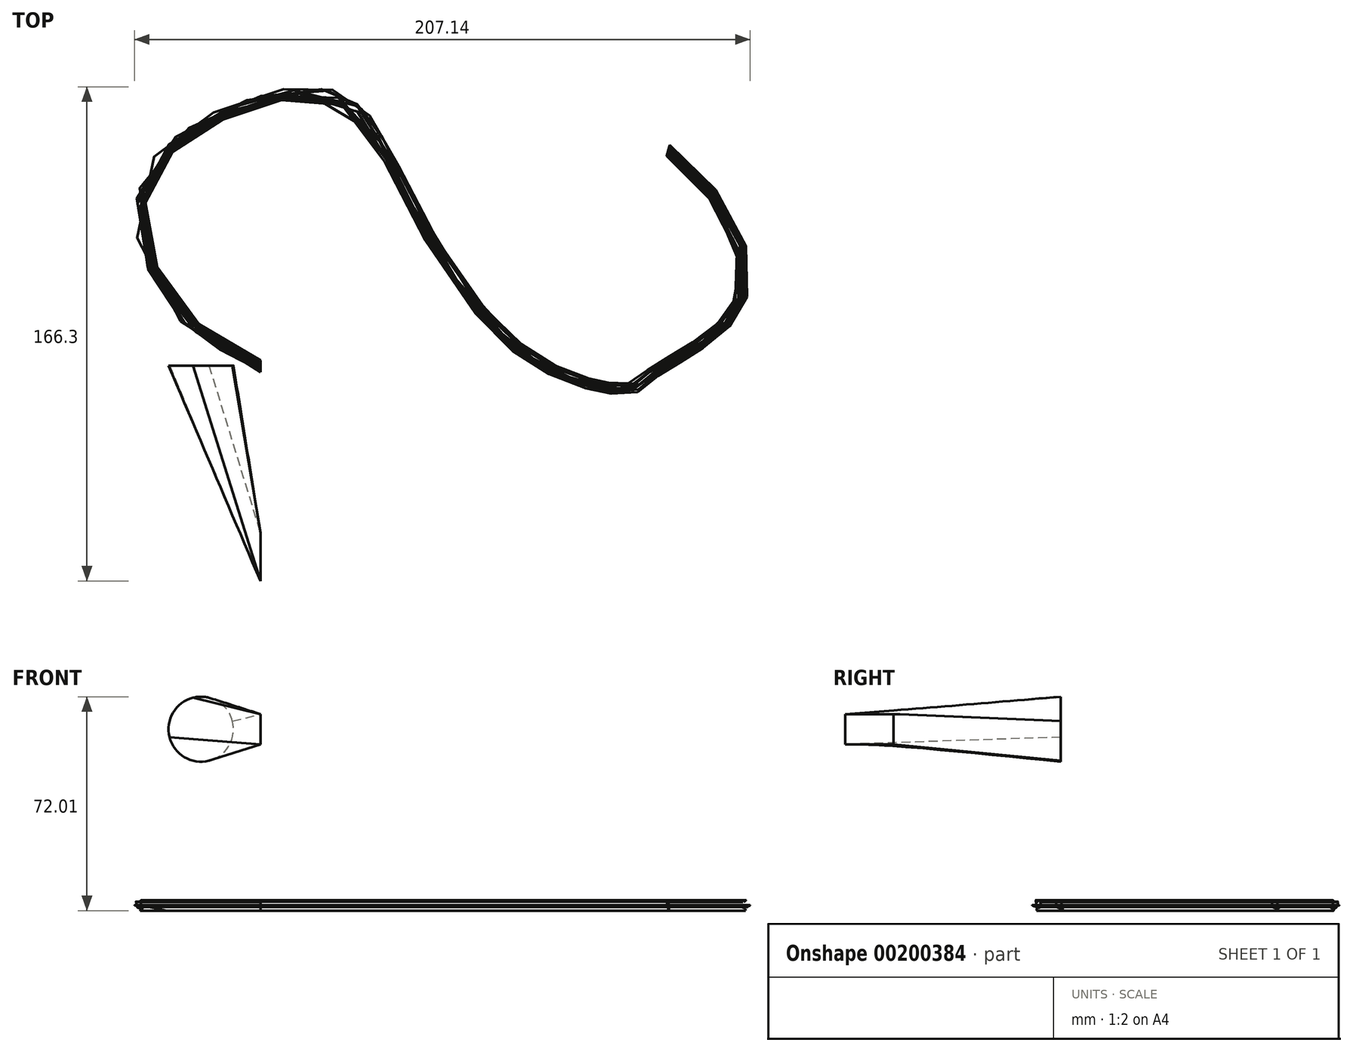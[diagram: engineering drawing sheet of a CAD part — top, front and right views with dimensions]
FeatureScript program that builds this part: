
annotation { "Feature Type Name" : "Feature", "Feature Type Description" : "" }
export const myFeature = defineFeature(function(context is Context, id is Id, definition is map)
    precondition{}
    {
        {
            var Q0;
            Q0=qCreatedBy(makeId("Front.planeOp"),FACE);
            var sketch = newSketch(context, id + "F0", { "sketchPlane" : qUnion([Q0])});
            skCircle(sketch, "E0", {"center": v(-20, 59.3) * mm, "radius": 10.93 * mm});
            skSolve(sketch);
        }
        {
            var Q0;
            Q0=qCreatedBy(makeId("Right.planeOp"),FACE);
            var sketch = newSketch(context, id + "F1", { "sketchPlane" : qUnion([Q0])});
            skLineSegment(sketch, "E1.bottom", {"start": v(-56.3, 64.38) * mm, "end": v(-72.5, 64.38) * mm});
            skLineSegment(sketch, "E1.top", {"start": v(-56.3, 54.2) * mm, "end": v(-72.5, 54.2) * mm});
            skLineSegment(sketch, "E1.left", {"start": v(-56.3, 64.38) * mm, "end": v(-56.3, 54.2) * mm});
            skLineSegment(sketch, "E1.right", {"start": v(-72.5, 64.38) * mm, "end": v(-72.5, 54.2) * mm});
            skSolve(sketch);
        }
        {
            var Q0;
            Q0=makeQuery(id+"F0.imprint","IMPRINT",FACE,{"disambiguationData":[TD([[makeQuery(id+"F0.imprint","IMPRINT",EDGE,{"derivedFrom":sQuery(id+"F0.wireOp",EDGE,"E0")}),1.0]])]});
            var Q1;
            Q1=makeQuery(id+"F1.imprint","IMPRINT",FACE,{"disambiguationData":[TD([[makeQuery(id+"F1.imprint","IMPRINT",EDGE,{"derivedFrom":sQuery(id+"F1.wireOp",EDGE,"E1.bottom")}),1.0]])]});
            loft(context, id + "F2", {"sheetProfilesArray" : [{ "sheetProfileEntities" : qUnion([Q0]) }, { "sheetProfileEntities" : qUnion([Q1]) }]});
        }
        {
            var Q0;
            Q0=qCreatedBy(makeId("Top.planeOp"),FACE);
            var sketch = newSketch(context, id + "F3", { "sketchPlane" : qUnion([Q0])});
            skFitSpline(sketch, "E2", {"points": [v(0, 0) * mm, v(-28.5, 19.67) * mm, v(-39.66, 58.21) * mm, v(-13.89, 84) * mm, v(26.27, 90.08) * mm, v(47.47, 60.64) * mm, v(90.2, 3.03) * mm, v(125.57, -7.63) * mm, v(131.45, -3.14) * mm, v(159.88, 18.4) * mm, v(157.7, 49.8) * mm, v(137.26, 72.64) * mm], "startDerivative": vector(-342.47, 165.12) * mm, "endDerivative": vector(-268.32, 236.1) * mm});
            skSolve(sketch);
        }
        {
            var Q0;
            Q0=qCreatedBy(makeId("Right.planeOp"),FACE);
            var sketch = newSketch(context, id + "F4", { "sketchPlane" : qUnion([Q0])});
            skFitSpline(sketch, "E3", {"points": [v(-0.64, 1.13) * mm, v(0.4, 1.71) * mm, v(0.36, 0.25) * mm, v(1.74, 0) * mm, v(0, -0.55) * mm, v(0.95, -0.58) * mm, v(0, -1.78) * mm, v(0, -1.22) * mm, v(-1.22, -0.66) * mm, v(-0.4, -0.4) * mm, v(-0.71, 0) * mm, v(-1.42, 0) * mm, v(-1.8, 0) * mm, v(-2.16, 0) * mm, v(-1.53, 0.52) * mm, v(-1.68, 1.23) * mm, v(-1.65, 1.23) * mm, v(-0.64, 1.13) * mm]});
            skSolve(sketch);
        }
        {
            var Q0;
            Q0 = qSketchRegion(id + "F4", true);
            var Q1;
            Q1 = qConstructionFilter(qBodyType(qCreatedBy(id + "F3" ,EDGE), BodyType.WIRE), ConstructionObject.NO);
            sweep(context, id + "F5", {"profiles" : qUnion([Q0]), "path" : qUnion([Q1])});
        }
    });
